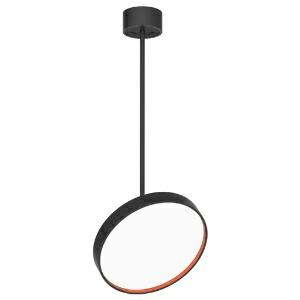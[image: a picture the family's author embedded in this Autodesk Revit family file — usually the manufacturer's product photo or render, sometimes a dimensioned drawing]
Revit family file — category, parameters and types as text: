
# Revit family: sign_diva_flex_korona_410-8702
name_source: partatom
category: Leuchten
revit_build: Autodesk Revit 2016 (Build: 20190508_0715(x64)
units: mm (PartAtom-declared; Revit-internal decimal feet)

## family parameters
Basisbauteil = Fläche
Beim Laden mit Abzugskörper schneiden = Nein
Bemaßung runder Anschluss = Durchmesser verwenden
Gemeinsam genutzt = Nein
Lichtquelle = Nein
Raumberechnungspunkt = Nein
Teiletyp = Normal

## types (1)
- 410-8702-D01-H27 (1 x LED, 2250 lm, 17.2 W, 2700K)
    Beschreibung = SIGN DIVA FLEX KORONA
    CIE Flux Codes = 47 78 95 100 80
    Color Rendering = 1A/90…99
    Color Temperature = 2700K
    Height = 870 mm
    Hersteller = Prolicht
    Lamp Light Flux = 2250 lm
    Lamp Power = 17.2 W
    Lamp count = 1
    Lampe = 1 x LED
    Length = 400 mm
    Luminous efficacy = 105 lm/W
    ModVariant = Nein
    Modell = 410-8702
    Mounting Place = Ceiling
    Mounting Type = Pendant
    Number of Poles = 1
    OnlyDefault = Ja
    Power Factor = 1
    Product Name = SIGN DIVA FLEX KORONA
    Product group = Suspended lights
    ProductGroupID = 941
    Protection Class = Protection class
    Protection Degree = Degree of protection
    RLX_Detail_Level = 1
    RlxData = <blob elided: 108217 chars, md5=1b0b4d32>
    Scheinlast = 17 VA
    Socket = socket
    Standby Power = 0 W
    System Light Flux = 1807 lm
    System Power = 17 W
    Typenbild = 410-8702.jpg
    Typenkommentare = DIFFUSER Opal (01),LED COLOUR DIR 2700 K (27)
    URL = http://relux.com
    VarID = 410-8702-d01-h27
    Voltage = 0 V
    Vorgabe-Ansicht = 1800 mm
    Weight = 0.00 kg
    Width = 0 mm  [stored 0 ft]

note: [stored X ft] marks values corroborated as IEEE doubles in the binary element streams (Revit-internal decimal feet)

## geometry (parser evidence)
native form markers: Sweep x14
no freeform markers — native parametric forms only
